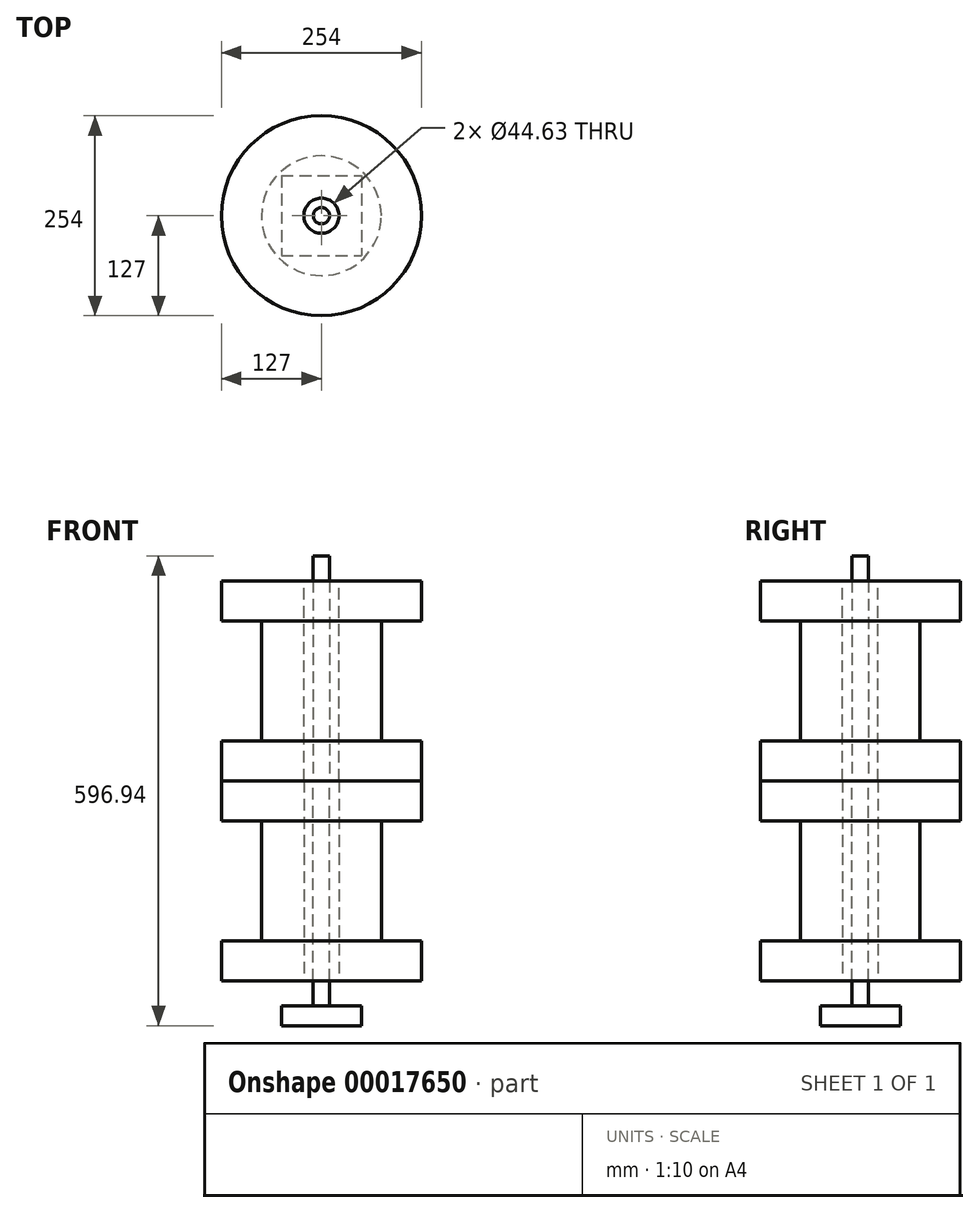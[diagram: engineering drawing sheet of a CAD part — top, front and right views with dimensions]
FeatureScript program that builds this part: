
annotation { "Feature Type Name" : "Feature", "Feature Type Description" : "" }
export const myFeature = defineFeature(function(context is Context, id is Id, definition is map)
    precondition{}
    {
        {
            var Q0;
            Q0=qCreatedBy(makeId("Top.planeOp"),FACE);
            var sketch = newSketch(context, id + "F0", { "sketchPlane" : qUnion([Q0])});
            skCircle(sketch, "E0", {"center": v(0, 0) * mm, "radius": 127 * mm});
            skSolve(sketch);
        }
        {
            var Q0;
            Q0=makeQuery(id+"F0.imprint","IMPRINT",FACE,{"disambiguationData":[TD([[makeQuery(id+"F0.imprint","IMPRINT",EDGE,{"derivedFrom":sQuery(id+"F0.wireOp",EDGE,"E0")}),1.0]])]});
            extrude(context, id + "F1", {"entities" : qUnion([Q0]), "depth" : 25.4 * mm});
        }
        {
            var Q0;
            Q0=makeQuery(id+"F1.opExtrude","CAP_FACE",FACE,{"disambiguationData":[OSD([sQuery(id+"F0.wireOp",EDGE,"E0")])],"isStart":false});
            extrude(context, id + "F2", {"entities" : qUnion([Q0]), "operationType" : NewBodyOperationType.ADD, "depth" : 25.4 * mm});
        }
        {
            var Q0;
            Q0=makeQuery(id+"F2.opExtrude","CAP_FACE",FACE,{"disambiguationData":[OSD([sQuery(id+"F0.wireOp",EDGE,"E0")])],"isStart":false});
            var sketch = newSketch(context, id + "F3", { "sketchPlane" : qUnion([Q0])});
            skCircle(sketch, "E1", {"center": v(0, 0) * mm, "radius": 76.14 * mm});
            skSolve(sketch);
        }
        {
            var Q0;
            Q0 = qSketchRegion(id + "F3", true);
            extrude(context, id + "F4", {"entities" : qUnion([Q0]), "operationType" : NewBodyOperationType.ADD, "depth" : 76.2 * mm});
        }
        {
            var Q0;
            Q0=makeQuery(id+"F1.opExtrude","SWEPT_BODY",BODY,{"disambiguationData":[OSD([sQuery(id+"F0.wireOp",EDGE,"E0")])]});
            var Q1;
            Q1=makeQuery(id+"F4.opExtrude","CAP_FACE",FACE,{"disambiguationData":[OSD([sQuery(id+"F3.wireOp",EDGE,"E1")])],"isStart":false});
            mirror(context, id + "F5", {"operationType" : NewBodyOperationType.ADD, "entities" : qUnion([Q0]), "mirrorPlane" : qUnion([Q1])});
        }
        {
            var Q0;
            Q0=makeQuery(id+"F5.opPattern","COPY",FACE,{"derivedFrom":makeQuery(id+"F1.opExtrude","CAP_FACE",FACE,{"disambiguationData":[OSD([sQuery(id+"F0.wireOp",EDGE,"E0")])],"isStart":true}),"instanceName":"1"});
            var sketch = newSketch(context, id + "F6", { "sketchPlane" : qUnion([Q0])});
            skCircle(sketch, "E2", {"center": v(0, 0) * mm, "radius": 17.47 * mm});
            skSolve(sketch);
        }
        {
            var Q0;
            Q0=sQuery(id+"F6.wireOp",VERTEX,"E2.center");
            var Q1;
            Q1=makeQuery(id+"F1.opExtrude","SWEPT_BODY",BODY,{"disambiguationData":[OSD([sQuery(id+"F0.wireOp",EDGE,"E0")])]});
            hole(context, id + "F7", {"style" : HoleStyle.SIMPLE, "holeDiameter" : 6.35 * mm, "endStyle" : HoleEndStyle.THROUGH, "locations" : qUnion([Q0]), "scope" : qUnion([Q1])});
        }
        {
            var Q0;
            Q0=makeQuery(id+"F5.opPattern","COPY",FACE,{"derivedFrom":makeQuery(id+"F1.opExtrude","CAP_FACE",FACE,{"disambiguationData":[OSD([sQuery(id+"F0.wireOp",EDGE,"E0")])],"isStart":true}),"instanceName":"1"});
            var sketch = newSketch(context, id + "F8", { "sketchPlane" : qUnion([Q0])});
            skCircle(sketch, "E3", {"center": v(0, 0) * mm, "radius": 22.32 * mm});
            skSolve(sketch);
        }
        {
            var Q0;
            Q0=makeQuery(id+"F8.imprint","IMPRINT",FACE,{"disambiguationData":[TD([[makeQuery(id+"F8.imprint","IMPRINT",EDGE,{"derivedFrom":sQuery(id+"F8.wireOp",EDGE,"E3")}),1.0]])]});
            extrude(context, id + "F9", {"entities" : qUnion([Q0]), "operationType" : NewBodyOperationType.REMOVE, "oppositeDirection" : true, "depth" : 277.65 * mm});
        }
        {
            var Q0;
            Q0=qCreatedBy(makeId("Top.planeOp"),FACE);
            var sketch = newSketch(context, id + "F10", { "sketchPlane" : qUnion([Q0])});
            skCircle(sketch, "E4", {"center": v(0, 0) * mm, "radius": 10.37 * mm});
            skSolve(sketch);
        }
        {
            var Q0;
            Q0=makeQuery(id+"F1.opExtrude","CAP_FACE",FACE,{"disambiguationData":[OSD([sQuery(id+"F0.wireOp",EDGE,"E0")])],"isStart":true});
            var sketch = newSketch(context, id + "F11", { "sketchPlane" : qUnion([Q0])});
            skSolve(sketch);
        }
        {
            var Q0;
            Q0 = qSketchRegion(id + "F11", true);
            var Q1;
            Q1=makeQuery(id+"F10.imprint","IMPRINT",FACE,{"disambiguationData":[TD([[makeQuery(id+"F10.imprint","IMPRINT",EDGE,{"derivedFrom":sQuery(id+"F10.wireOp",EDGE,"E4")}),1.0]])]});
            extrude(context, id + "F12", {"entities" : qUnion([Q0, Q1]), "depth" : 285.77 * mm});
        }
        {
            var Q0;
            Q0=makeQuery(id+"F12.opExtrude","SWEPT_BODY",BODY,{"disambiguationData":[OSD([sQuery(id+"F10.wireOp",EDGE,"E4")])]});
            var Q1;
            Q1=makeQuery(id+"F1.opExtrude","SWEPT_BODY",BODY,{"disambiguationData":[OSD([sQuery(id+"F0.wireOp",EDGE,"E0")])]});
            var Q2;
            Q2=makeQuery(id+"F11.imprint","IMPRINT",FACE,{"disambiguationData":[TD([[makeQuery(id+"F11.imprint","IMPRINT",EDGE,{"derivedFrom":makeQuery(id+"F9.boolean.opBoolean","INTERSECT",EDGE,{"derivedFrom":[makeQuery(id+"F1.opExtrude","CAP_FACE",FACE,{"disambiguationData":[OSD([sQuery(id+"F0.wireOp",EDGE,"E0")])],"isStart":true}),makeQuery(id+"F9.opExtrude","SWEPT_FACE",FACE,{"disambiguationData":[OSD([sQuery(id+"F8.wireOp",EDGE,"E3")])]})]})}),-1.0]])]});
            mirror(context, id + "F13", {"entities" : qUnion([Q0, Q1]), "mirrorPlane" : qUnion([Q2])});
        }
        {
            var Q0;
            Q0=makeQuery(id+"F13.opPattern","COPY",FACE,{"derivedFrom":makeQuery(id+"F12.opExtrude","CAP_FACE",FACE,{"disambiguationData":[OSD([sQuery(id+"F10.wireOp",EDGE,"E4")])],"isStart":false}),"instanceName":"1"});
            var sketch = newSketch(context, id + "F14", { "sketchPlane" : qUnion([Q0])});
            skLineSegment(sketch, "E5.bottom", {"start": v(-50.8, -50.8) * mm, "end": v(50.8, -50.8) * mm});
            skLineSegment(sketch, "E5.top", {"start": v(-50.8, 50.8) * mm, "end": v(50.8, 50.8) * mm});
            skLineSegment(sketch, "E5.left", {"start": v(-50.8, -50.8) * mm, "end": v(-50.8, 50.8) * mm});
            skLineSegment(sketch, "E5.right", {"start": v(50.8, -50.8) * mm, "end": v(50.8, 50.8) * mm});
            skSolve(sketch);
        }
        {
            var Q0;
            Q0=sQuery(id+"F14.wireOp",EDGE,"E5.bottom");
            extrude(context, id + "F15", {"bodyType" : ToolBodyType.SURFACE, "surfaceEntities" : qUnion([Q0]), "depth" : 25.4 * mm});
        }
        {
            var Q0;
            Q0 = qSketchRegion(id + "F14", true);
            extrude(context, id + "F16", {"entities" : qUnion([Q0]), "operationType" : NewBodyOperationType.ADD, "depth" : 25.4 * mm});
        }
    });
